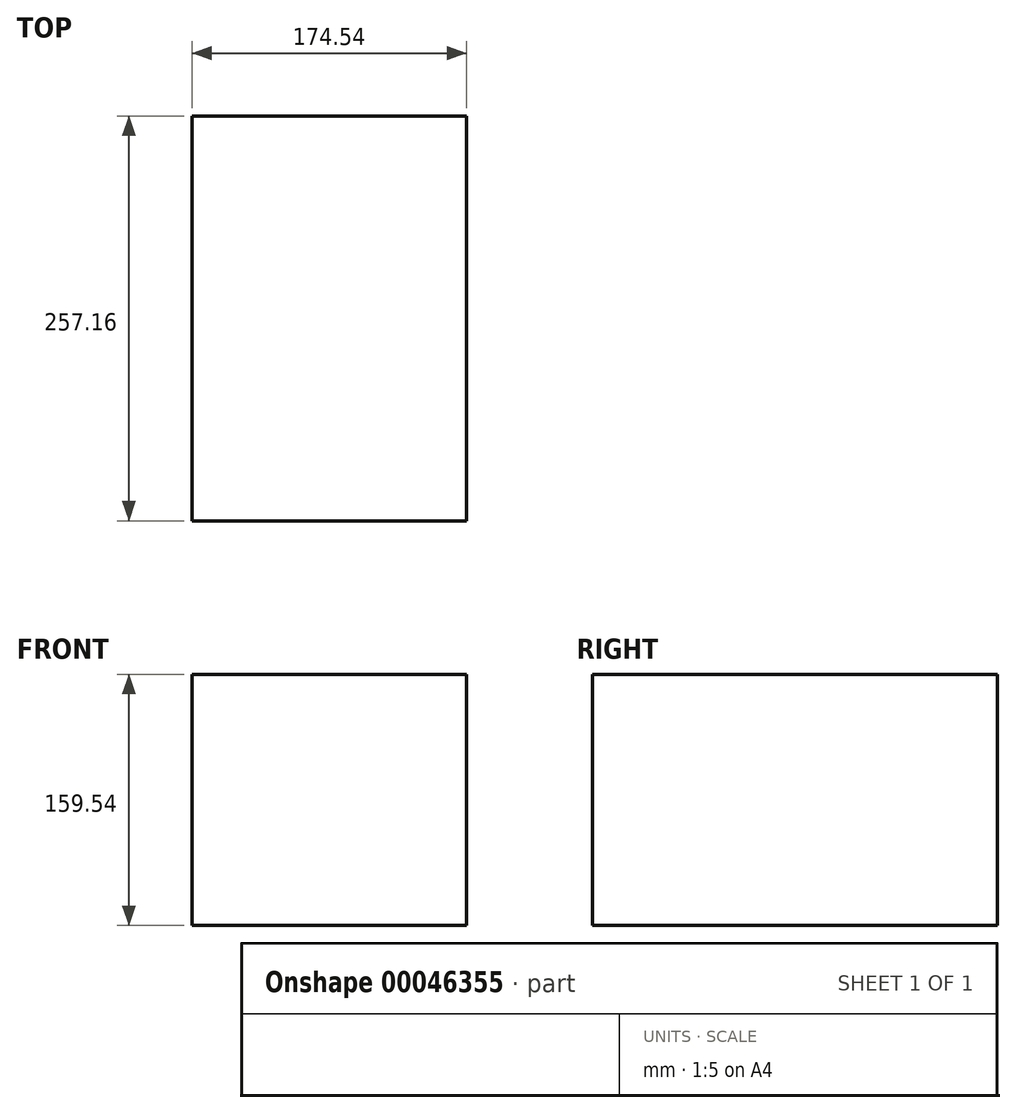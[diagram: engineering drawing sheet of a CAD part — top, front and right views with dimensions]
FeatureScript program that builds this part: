
annotation { "Feature Type Name" : "Feature", "Feature Type Description" : "" }
export const myFeature = defineFeature(function(context is Context, id is Id, definition is map)
    precondition{}
    {
        {
            var Q0;
            Q0=qCreatedBy(makeId("Front.planeOp"),FACE);
            var sketch = newSketch(context, id + "F0", { "sketchPlane" : qUnion([Q0])});
            skLineSegment(sketch, "E0.rect.bottom", {"start": v(87.27, -79.77) * mm, "end": v(-87.27, -79.77) * mm});
            skLineSegment(sketch, "E0.rect.top", {"start": v(87.27, 79.77) * mm, "end": v(-87.27, 79.77) * mm});
            skLineSegment(sketch, "E0.rect.left", {"start": v(87.27, -79.77) * mm, "end": v(87.27, 79.77) * mm});
            skLineSegment(sketch, "E0.rect.right", {"start": v(-87.27, -79.77) * mm, "end": v(-87.27, 79.77) * mm});
            skPoint(sketch, "E0.rect.middle", {"position": v(0, 0) * mm});
            skSolve(sketch);
        }
        {
            var Q0;
            Q0 = qSketchRegion(id + "F0", true);
            extrude(context, id + "F1", {"entities" : qUnion([Q0]), "depth" : 160.48 * mm});
        }
        {
            var Q0;
            Q0=makeQuery(id+"F1.opExtrude","CAP_FACE",FACE,{"disambiguationData":[OSD([sQuery(id+"F0.wireOp",EDGE,"E0.rect.bottom"),sQuery(id+"F0.wireOp",EDGE,"E0.rect.top"),sQuery(id+"F0.wireOp",EDGE,"E0.rect.left"),sQuery(id+"F0.wireOp",EDGE,"E0.rect.right")])],"isStart":true});
            extrude(context, id + "F2", {"entities" : qUnion([Q0]), "operationType" : NewBodyOperationType.ADD, "depth" : 96.68 * mm});
        }
    });
